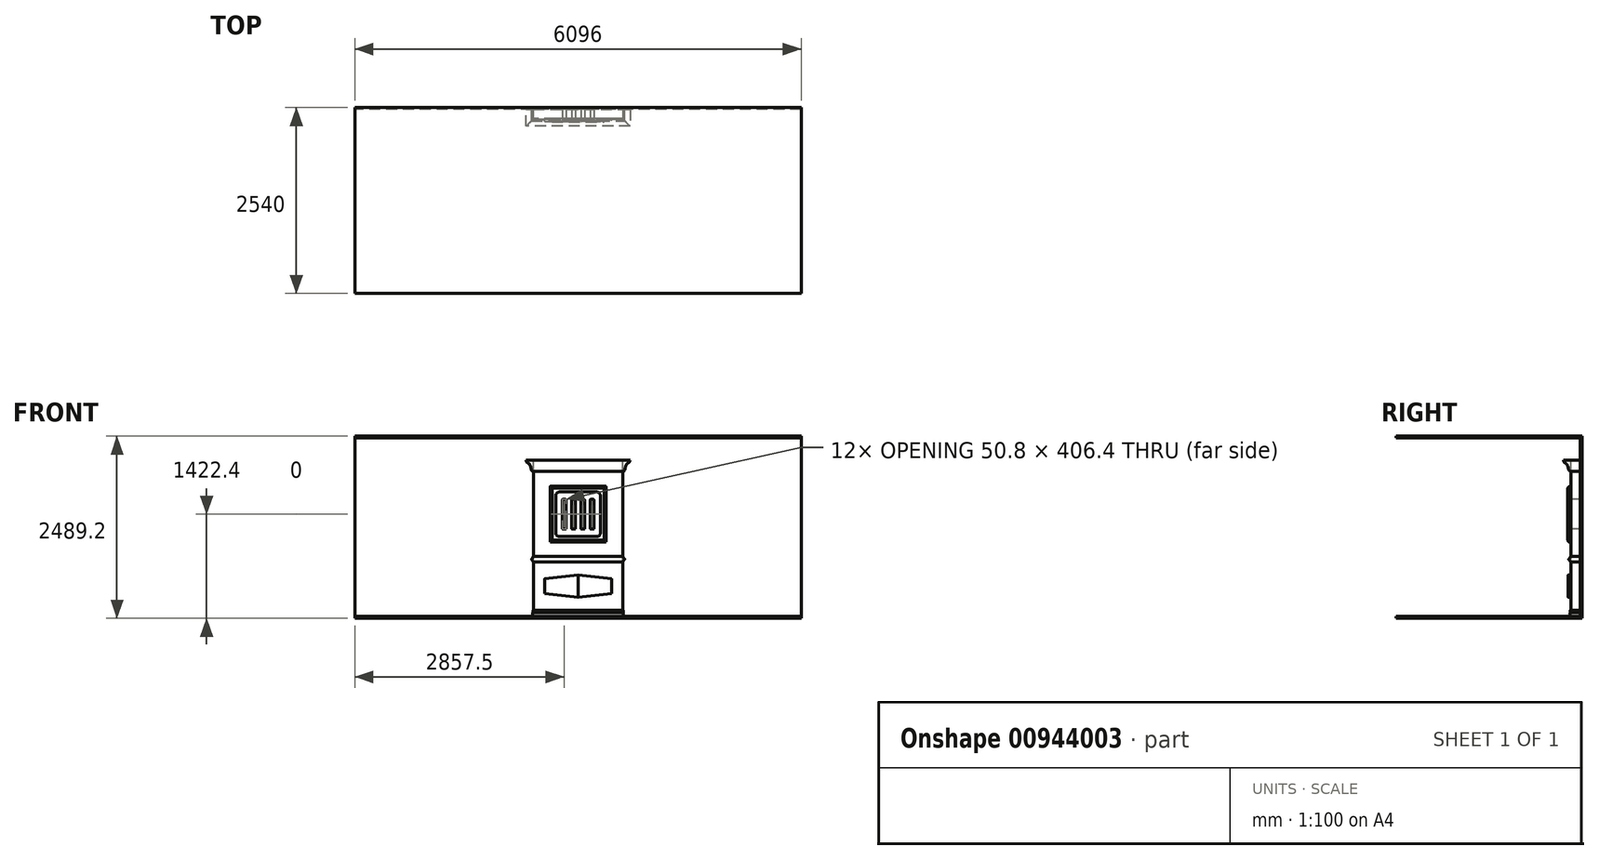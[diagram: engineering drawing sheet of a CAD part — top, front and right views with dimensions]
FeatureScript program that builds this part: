
annotation { "Feature Type Name" : "Feature", "Feature Type Description" : "" }
export const myFeature = defineFeature(function(context is Context, id is Id, definition is map)
    precondition{}
    {
        {
            var Q0;
            Q0=qCreatedBy(makeId("Front.planeOp"),FACE);
            var sketch = newSketch(context, id + "F0", { "sketchPlane" : qUnion([Q0])});
            skLineSegment(sketch, "E0.bottom", {"start": v(0, 0) * mm, "end": v(3657.6, 0) * mm});
            skLineSegment(sketch, "E0.top", {"start": v(0, 2438.4) * mm, "end": v(3657.6, 2438.4) * mm});
            skLineSegment(sketch, "E0.left", {"start": v(0, 0) * mm, "end": v(0, 2438.4) * mm});
            skLineSegment(sketch, "E0.right", {"start": v(3657.6, 0) * mm, "end": v(3657.6, 2438.4) * mm});
            skLineSegment(sketch, "E1.bottom", {"start": v(0, 0) * mm, "end": v(-2438.4, 0) * mm});
            skLineSegment(sketch, "E1.top", {"start": v(0, 2438.4) * mm, "end": v(-2438.4, 2438.4) * mm});
            skLineSegment(sketch, "E1.right", {"start": v(-2438.4, 0) * mm, "end": v(-2438.4, 2438.4) * mm});
            skSolve(sketch);
        }
        {
            var Q0;
            Q0=makeQuery(id+"F0.imprint","IMPRINT",FACE,{"disambiguationData":[TD([[makeQuery(id+"F0.imprint","IMPRINT",EDGE,{"derivedFrom":sQuery(id+"F0.wireOp",EDGE,"E1.bottom")}),-1.0]])]});
            var Q1;
            Q1=makeQuery(id+"F0.imprint","IMPRINT",FACE,{"disambiguationData":[TD([[makeQuery(id+"F0.imprint","IMPRINT",EDGE,{"derivedFrom":sQuery(id+"F0.wireOp",EDGE,"E0.bottom")}),1.0]])]});
            var Q2;
            Q2 = qConstructionFilter(qBodyType(qCreatedBy(id + "F0" ,EDGE), BodyType.WIRE), ConstructionObject.NO);
            extrude(context, id + "F1", {"entities" : qUnion([Q0, Q1]), "surfaceEntities" : qUnion([Q2]), "oppositeDirection" : true, "depth" : 25.4 * mm, "offsetDistance" : 25.4 * mm});
        }
        {
            var Q0;
            Q0=makeQuery(id+"F1.opExtrude","SWEPT_FACE",FACE,{"disambiguationData":[OSD([sQuery(id+"F0.wireOp",EDGE,"E0.top"),sQuery(id+"F0.wireOp",EDGE,"E1.top")])]});
            var sketch = newSketch(context, id + "F2", { "sketchPlane" : qUnion([Q0])});
            skLineSegment(sketch, "E2.bottom", {"start": v(-2438.4, 25.4) * mm, "end": v(3657.6, 25.4) * mm});
            skLineSegment(sketch, "E2.top", {"start": v(-2438.4, -2514.6) * mm, "end": v(3657.6, -2514.6) * mm});
            skLineSegment(sketch, "E2.left", {"start": v(-2438.4, 25.4) * mm, "end": v(-2438.4, -2514.6) * mm});
            skLineSegment(sketch, "E2.right", {"start": v(3657.6, 25.4) * mm, "end": v(3657.6, -2514.6) * mm});
            skSolve(sketch);
        }
        {
            var Q0;
            Q0 = qSketchRegion(id + "F2", true);
            extrude(context, id + "F3", {"entities" : qUnion([Q0]), "operationType" : NewBodyOperationType.ADD, "depth" : 25.4 * mm, "offsetDistance" : 25.4 * mm});
        }
        {
            var Q0;
            Q0=makeQuery(id+"F1.opExtrude","SWEPT_FACE",FACE,{"disambiguationData":[OSD([sQuery(id+"F0.wireOp",EDGE,"E0.bottom"),sQuery(id+"F0.wireOp",EDGE,"E1.bottom")])]});
            var sketch = newSketch(context, id + "F4", { "sketchPlane" : qUnion([Q0])});
            skLineSegment(sketch, "E3.bottom", {"start": v(-2438.4, -25.4) * mm, "end": v(3657.6, -25.4) * mm});
            skLineSegment(sketch, "E3.top", {"start": v(-2438.4, 2514.6) * mm, "end": v(3657.6, 2514.6) * mm});
            skLineSegment(sketch, "E3.left", {"start": v(-2438.4, -25.4) * mm, "end": v(-2438.4, 2514.6) * mm});
            skLineSegment(sketch, "E3.right", {"start": v(3657.6, -25.4) * mm, "end": v(3657.6, 2514.6) * mm});
            skSolve(sketch);
        }
        {
            var Q0;
            Q0 = qSketchRegion(id + "F4", true);
            extrude(context, id + "F5", {"entities" : qUnion([Q0]), "operationType" : NewBodyOperationType.ADD, "depth" : 25.4 * mm, "offsetDistance" : 25.4 * mm});
        }
        {
            var Q0;
            Q0=qCreatedBy(makeId("Front.planeOp"),FACE);
            var sketch = newSketch(context, id + "F6", { "sketchPlane" : qUnion([Q0])});
            skLineSegment(sketch, "E4.bottom", {"start": v(0, 0) * mm, "end": v(1219.2, 0) * mm});
            skLineSegment(sketch, "E4.top", {"start": v(0, 2133.6) * mm, "end": v(1219.2, 2133.6) * mm});
            skLineSegment(sketch, "E4.left", {"start": v(0, 0) * mm, "end": v(0, 2133.6) * mm});
            skLineSegment(sketch, "E4.right", {"start": v(1219.2, 0) * mm, "end": v(1219.2, 2133.6) * mm});
            skSolve(sketch);
        }
        {
            var Q0;
            Q0 = qSketchRegion(id + "F6", true);
            extrude(context, id + "F7", {"entities" : qUnion([Q0]), "depth" : 127 * mm, "offsetDistance" : 25.4 * mm});
        }
        {
            var Q0;
            Q0=makeQuery(id+"F7.opExtrude","CAP_FACE",FACE,{"disambiguationData":[OSD([sQuery(id+"F6.wireOp",EDGE,"E4.bottom"),sQuery(id+"F6.wireOp",EDGE,"E4.top"),sQuery(id+"F6.wireOp",EDGE,"E4.left"),sQuery(id+"F6.wireOp",EDGE,"E4.right")])],"isStart":false});
            var sketch = newSketch(context, id + "F8", { "sketchPlane" : qUnion([Q0])});
            skLineSegment(sketch, "E5.bottom", {"start": v(228.6, 1016) * mm, "end": v(990.6, 1016) * mm});
            skLineSegment(sketch, "E5.top", {"start": v(228.6, 1778) * mm, "end": v(990.6, 1778) * mm});
            skLineSegment(sketch, "E5.left", {"start": v(228.6, 1016) * mm, "end": v(228.6, 1778) * mm});
            skLineSegment(sketch, "E5.right", {"start": v(990.6, 1016) * mm, "end": v(990.6, 1778) * mm});
            skPoint(sketch, "E6", {"position": v(609.6, 1778) * mm});
            skPoint(sketch, "E7", {"position": v(609.6, 2133.6) * mm});
            skSolve(sketch);
        }
        {
            var Q0;
            Q0 = qSketchRegion(id + "F8", true);
            extrude(context, id + "F9", {"entities" : qUnion([Q0]), "depth" : 38.1 * mm, "offsetDistance" : 25.4 * mm});
        }
        {
            var Q0;
            Q0=makeQuery(id+"F7.opExtrude","SWEPT_FACE",FACE,{"disambiguationData":[OSD([sQuery(id+"F6.wireOp",EDGE,"E4.right")])]});
            var sketch = newSketch(context, id + "F10", { "sketchPlane" : qUnion([Q0])});
            skFitSpline(sketch, "E8", {"points": [v(-127, 1981.2) * mm, v(-163.97, 2045.51) * mm, v(-194.3, 2094.8) * mm, v(-228.6, 2133.6) * mm], "startDerivative": vector(-269.16, 89.83) * mm, "endDerivative": vector(-112.82, 304.77) * mm});
            skLineSegment(sketch, "E9", {"start": v(-228.6, 2133.6) * mm, "end": v(-127, 2133.6) * mm});
            skLineSegment(sketch, "E10", {"start": v(-127, 2133.6) * mm, "end": v(-127, 1981.2) * mm});
            skSolve(sketch);
        }
        {
            var Q0;
            Q0=makeQuery(id+"F10.imprint","IMPRINT",FACE,{"disambiguationData":[TD([[makeQuery(id+"F10.imprint","IMPRINT",EDGE,{"derivedFrom":sQuery(id+"F10.wireOp",EDGE,"E8")}),-1.0]])]});
            var Q1;
            Q1=makeQuery(id+"F7.opExtrude","CAP_EDGE",EDGE,{"disambiguationData":[OSD([sQuery(id+"F6.wireOp",EDGE,"E4.top")])],"isStart":false});
            var Q2;
            Q2=makeQuery(id+"F7.opExtrude","SWEPT_EDGE",EDGE,{"disambiguationData":[OSD([sQuery(id+"F6.wireOp",EDGE,"E4.top"),sQuery(id+"F6.wireOp",EDGE,"E4.left")])]});
            var Q3;
            Q3=makeQuery(id+"F7.opExtrude","SWEPT_EDGE",EDGE,{"disambiguationData":[OSD([sQuery(id+"F6.wireOp",EDGE,"E4.top"),sQuery(id+"F6.wireOp",EDGE,"E4.right")])]});
            sweep(context, id + "F11", {"profiles" : qUnion([Q0]), "path" : qUnion([Q1, Q2, Q3])});
        }
        {
            var Q0;
            Q0=makeQuery(id+"F9.opExtrude","SWEPT_FACE",FACE,{"disambiguationData":[OSD([sQuery(id+"F8.wireOp",EDGE,"E5.right")])]});
            var sketch = newSketch(context, id + "F12", { "sketchPlane" : qUnion([Q0])});
            skArc(sketch, "E11", {"start": v(-165.1, 1778) * mm, "mid": v(-153.94, 1804.94) * mm, "end": v(-127, 1816.1) * mm});
            skLineSegment(sketch, "E12", {"start": v(-127, 1816.1) * mm, "end": v(-127, 1778) * mm});
            skLineSegment(sketch, "E13", {"start": v(-165.1, 1778) * mm, "end": v(-127, 1778) * mm});
            skSolve(sketch);
        }
        {
            var Q0;
            Q0=makeQuery(id+"F9.opExtrude","CAP_FACE",FACE,{"disambiguationData":[OSD([sQuery(id+"F8.wireOp",EDGE,"E5.bottom"),sQuery(id+"F8.wireOp",EDGE,"E5.top"),sQuery(id+"F8.wireOp",EDGE,"E5.left"),sQuery(id+"F8.wireOp",EDGE,"E5.right")])],"isStart":false});
            var sketch = newSketch(context, id + "F13", { "sketchPlane" : qUnion([Q0])});
            skLineSegment(sketch, "E14.bottom", {"start": v(406.4, 1625.6) * mm, "end": v(431.8, 1625.6) * mm});
            skLineSegment(sketch, "E14.top", {"start": v(406.4, 1447.8) * mm, "end": v(431.8, 1447.8) * mm});
            skLineSegment(sketch, "E14.left", {"start": v(406.4, 1625.6) * mm, "end": v(406.4, 1447.8) * mm});
            skLineSegment(sketch, "E14.right", {"start": v(431.8, 1625.6) * mm, "end": v(431.8, 1447.8) * mm});
            skArc(sketch, "E15", {"start": v(431.8, 1625.6) * mm, "mid": v(419.1, 1638.3) * mm, "end": v(406.4, 1625.6) * mm});
            skArc(sketch, "E16", {"start": v(406.4, 1447.8) * mm, "mid": v(419.1, 1435.1) * mm, "end": v(431.8, 1447.8) * mm});
            skPoint(sketch, "E17", {"position": v(609.6, 1778) * mm});
            skLineSegment(sketch, "E18.0.1.0", {"start": v(406.4, 1346.2) * mm, "end": v(406.4, 1168.4) * mm});
            skArc(sketch, "E18.0.1.1", {"start": v(431.8, 1346.2) * mm, "mid": v(419.1, 1358.9) * mm, "end": v(406.4, 1346.2) * mm});
            skLineSegment(sketch, "E18.0.1.2", {"start": v(431.8, 1346.2) * mm, "end": v(431.8, 1168.4) * mm});
            skLineSegment(sketch, "E18.0.1.3", {"start": v(406.4, 1346.2) * mm, "end": v(431.8, 1346.2) * mm});
            skArc(sketch, "E18.0.1.4", {"start": v(406.4, 1168.4) * mm, "mid": v(419.1, 1155.7) * mm, "end": v(431.8, 1168.4) * mm});
            skLineSegment(sketch, "E18.0.1.5", {"start": v(406.4, 1168.4) * mm, "end": v(431.8, 1168.4) * mm});
            skLineSegment(sketch, "E18.1.0.0", {"start": v(482.6, 1625.6) * mm, "end": v(482.6, 1447.8) * mm});
            skArc(sketch, "E18.1.0.1", {"start": v(508, 1625.6) * mm, "mid": v(495.3, 1638.3) * mm, "end": v(482.6, 1625.6) * mm});
            skLineSegment(sketch, "E18.1.0.2", {"start": v(508, 1625.6) * mm, "end": v(508, 1447.8) * mm});
            skLineSegment(sketch, "E18.1.0.3", {"start": v(482.6, 1625.6) * mm, "end": v(508, 1625.6) * mm});
            skArc(sketch, "E18.1.0.4", {"start": v(482.6, 1447.8) * mm, "mid": v(495.3, 1435.1) * mm, "end": v(508, 1447.8) * mm});
            skLineSegment(sketch, "E18.1.0.5", {"start": v(482.6, 1447.8) * mm, "end": v(508, 1447.8) * mm});
            skLineSegment(sketch, "E18.1.1.0", {"start": v(482.6, 1346.2) * mm, "end": v(482.6, 1168.4) * mm});
            skArc(sketch, "E18.1.1.1", {"start": v(508, 1346.2) * mm, "mid": v(495.3, 1358.9) * mm, "end": v(482.6, 1346.2) * mm});
            skLineSegment(sketch, "E18.1.1.2", {"start": v(508, 1346.2) * mm, "end": v(508, 1168.4) * mm});
            skLineSegment(sketch, "E18.1.1.3", {"start": v(482.6, 1346.2) * mm, "end": v(508, 1346.2) * mm});
            skArc(sketch, "E18.1.1.4", {"start": v(482.6, 1168.4) * mm, "mid": v(495.3, 1155.7) * mm, "end": v(508, 1168.4) * mm});
            skLineSegment(sketch, "E18.1.1.5", {"start": v(482.6, 1168.4) * mm, "end": v(508, 1168.4) * mm});
            skLineSegment(sketch, "E18.2.0.0", {"start": v(558.8, 1625.6) * mm, "end": v(558.8, 1447.8) * mm});
            skArc(sketch, "E18.2.0.1", {"start": v(584.2, 1625.6) * mm, "mid": v(571.5, 1638.3) * mm, "end": v(558.8, 1625.6) * mm});
            skLineSegment(sketch, "E18.2.0.2", {"start": v(584.2, 1625.6) * mm, "end": v(584.2, 1447.8) * mm});
            skLineSegment(sketch, "E18.2.0.3", {"start": v(558.8, 1625.6) * mm, "end": v(584.2, 1625.6) * mm});
            skArc(sketch, "E18.2.0.4", {"start": v(558.8, 1447.8) * mm, "mid": v(571.5, 1435.1) * mm, "end": v(584.2, 1447.8) * mm});
            skLineSegment(sketch, "E18.2.0.5", {"start": v(558.8, 1447.8) * mm, "end": v(584.2, 1447.8) * mm});
            skLineSegment(sketch, "E18.2.1.0", {"start": v(558.8, 1346.2) * mm, "end": v(558.8, 1168.4) * mm});
            skArc(sketch, "E18.2.1.1", {"start": v(584.2, 1346.2) * mm, "mid": v(571.5, 1358.9) * mm, "end": v(558.8, 1346.2) * mm});
            skLineSegment(sketch, "E18.2.1.2", {"start": v(584.2, 1346.2) * mm, "end": v(584.2, 1168.4) * mm});
            skLineSegment(sketch, "E18.2.1.3", {"start": v(558.8, 1346.2) * mm, "end": v(584.2, 1346.2) * mm});
            skArc(sketch, "E18.2.1.4", {"start": v(558.8, 1168.4) * mm, "mid": v(571.5, 1155.7) * mm, "end": v(584.2, 1168.4) * mm});
            skLineSegment(sketch, "E18.2.1.5", {"start": v(558.8, 1168.4) * mm, "end": v(584.2, 1168.4) * mm});
            skLineSegment(sketch, "E18.3.0.0", {"start": v(635, 1625.6) * mm, "end": v(635, 1447.8) * mm});
            skArc(sketch, "E18.3.0.1", {"start": v(660.4, 1625.6) * mm, "mid": v(647.7, 1638.3) * mm, "end": v(635, 1625.6) * mm});
            skLineSegment(sketch, "E18.3.0.2", {"start": v(660.4, 1625.6) * mm, "end": v(660.4, 1447.8) * mm});
            skLineSegment(sketch, "E18.3.0.3", {"start": v(635, 1625.6) * mm, "end": v(660.4, 1625.6) * mm});
            skArc(sketch, "E18.3.0.4", {"start": v(635, 1447.8) * mm, "mid": v(647.7, 1435.1) * mm, "end": v(660.4, 1447.8) * mm});
            skLineSegment(sketch, "E18.3.0.5", {"start": v(635, 1447.8) * mm, "end": v(660.4, 1447.8) * mm});
            skLineSegment(sketch, "E18.3.1.0", {"start": v(635, 1346.2) * mm, "end": v(635, 1168.4) * mm});
            skArc(sketch, "E18.3.1.1", {"start": v(660.4, 1346.2) * mm, "mid": v(647.7, 1358.9) * mm, "end": v(635, 1346.2) * mm});
            skLineSegment(sketch, "E18.3.1.2", {"start": v(660.4, 1346.2) * mm, "end": v(660.4, 1168.4) * mm});
            skLineSegment(sketch, "E18.3.1.3", {"start": v(635, 1346.2) * mm, "end": v(660.4, 1346.2) * mm});
            skArc(sketch, "E18.3.1.4", {"start": v(635, 1168.4) * mm, "mid": v(647.7, 1155.7) * mm, "end": v(660.4, 1168.4) * mm});
            skLineSegment(sketch, "E18.3.1.5", {"start": v(635, 1168.4) * mm, "end": v(660.4, 1168.4) * mm});
            skLineSegment(sketch, "E18.4.0.0", {"start": v(711.2, 1625.6) * mm, "end": v(711.2, 1447.8) * mm});
            skArc(sketch, "E18.4.0.1", {"start": v(736.6, 1625.6) * mm, "mid": v(723.9, 1638.3) * mm, "end": v(711.2, 1625.6) * mm});
            skLineSegment(sketch, "E18.4.0.2", {"start": v(736.6, 1625.6) * mm, "end": v(736.6, 1447.8) * mm});
            skLineSegment(sketch, "E18.4.0.3", {"start": v(711.2, 1625.6) * mm, "end": v(736.6, 1625.6) * mm});
            skArc(sketch, "E18.4.0.4", {"start": v(711.2, 1447.8) * mm, "mid": v(723.9, 1435.1) * mm, "end": v(736.6, 1447.8) * mm});
            skLineSegment(sketch, "E18.4.0.5", {"start": v(711.2, 1447.8) * mm, "end": v(736.6, 1447.8) * mm});
            skLineSegment(sketch, "E18.4.1.0", {"start": v(711.2, 1346.2) * mm, "end": v(711.2, 1168.4) * mm});
            skArc(sketch, "E18.4.1.1", {"start": v(736.6, 1346.2) * mm, "mid": v(723.9, 1358.9) * mm, "end": v(711.2, 1346.2) * mm});
            skLineSegment(sketch, "E18.4.1.2", {"start": v(736.6, 1346.2) * mm, "end": v(736.6, 1168.4) * mm});
            skLineSegment(sketch, "E18.4.1.3", {"start": v(711.2, 1346.2) * mm, "end": v(736.6, 1346.2) * mm});
            skArc(sketch, "E18.4.1.4", {"start": v(711.2, 1168.4) * mm, "mid": v(723.9, 1155.7) * mm, "end": v(736.6, 1168.4) * mm});
            skLineSegment(sketch, "E18.4.1.5", {"start": v(711.2, 1168.4) * mm, "end": v(736.6, 1168.4) * mm});
            skLineSegment(sketch, "E18.5.0.0", {"start": v(787.4, 1625.6) * mm, "end": v(787.4, 1447.8) * mm});
            skArc(sketch, "E18.5.0.1", {"start": v(812.8, 1625.6) * mm, "mid": v(800.1, 1638.3) * mm, "end": v(787.4, 1625.6) * mm});
            skLineSegment(sketch, "E18.5.0.2", {"start": v(812.8, 1625.6) * mm, "end": v(812.8, 1447.8) * mm});
            skLineSegment(sketch, "E18.5.0.3", {"start": v(787.4, 1625.6) * mm, "end": v(812.8, 1625.6) * mm});
            skArc(sketch, "E18.5.0.4", {"start": v(787.4, 1447.8) * mm, "mid": v(800.1, 1435.1) * mm, "end": v(812.8, 1447.8) * mm});
            skLineSegment(sketch, "E18.5.0.5", {"start": v(787.4, 1447.8) * mm, "end": v(812.8, 1447.8) * mm});
            skLineSegment(sketch, "E18.5.1.0", {"start": v(787.4, 1346.2) * mm, "end": v(787.4, 1168.4) * mm});
            skArc(sketch, "E18.5.1.1", {"start": v(812.8, 1346.2) * mm, "mid": v(800.1, 1358.9) * mm, "end": v(787.4, 1346.2) * mm});
            skLineSegment(sketch, "E18.5.1.2", {"start": v(812.8, 1346.2) * mm, "end": v(812.8, 1168.4) * mm});
            skLineSegment(sketch, "E18.5.1.3", {"start": v(787.4, 1346.2) * mm, "end": v(812.8, 1346.2) * mm});
            skArc(sketch, "E18.5.1.4", {"start": v(787.4, 1168.4) * mm, "mid": v(800.1, 1155.7) * mm, "end": v(812.8, 1168.4) * mm});
            skLineSegment(sketch, "E18.5.1.5", {"start": v(787.4, 1168.4) * mm, "end": v(812.8, 1168.4) * mm});
            skLineSegment(sketch, "E18.direction1", {"start": v(406.4, 1447.8) * mm, "end": v(482.6, 1447.8) * mm, "construction": true});
            skLineSegment(sketch, "E18.direction2", {"start": v(406.4, 1447.8) * mm, "end": v(406.4, 1168.4) * mm, "construction": true});
            skLineSegment(sketch, "E19", {"start": v(584.2, 1536.7) * mm, "end": v(635, 1536.7) * mm, "construction": true});
            skPoint(sketch, "E20", {"position": v(609.6, 1536.7) * mm});
            skLineSegment(sketch, "E21", {"start": v(419.1, 1447.8) * mm, "end": v(419.1, 1346.2) * mm, "construction": true});
            skPoint(sketch, "E22", {"position": v(419.1, 1397) * mm});
            skPoint(sketch, "E23", {"position": v(228.6, 1397) * mm});
            skSolve(sketch);
        }
        {
            var Q0;
            Q0=makeQuery(id+"F9.opExtrude","CAP_FACE",FACE,{"disambiguationData":[OSD([sQuery(id+"F8.wireOp",EDGE,"E5.bottom"),sQuery(id+"F8.wireOp",EDGE,"E5.top"),sQuery(id+"F8.wireOp",EDGE,"E5.left"),sQuery(id+"F8.wireOp",EDGE,"E5.right")])],"isStart":false});
            var sketch = newSketch(context, id + "F14", { "sketchPlane" : qUnion([Q0])});
            skLineSegment(sketch, "E24.bottom", {"start": v(438.15, 1600.2) * mm, "end": v(400.05, 1600.2) * mm});
            skLineSegment(sketch, "E24.top", {"start": v(438.15, 1193.8) * mm, "end": v(400.05, 1193.8) * mm});
            skLineSegment(sketch, "E24.left", {"start": v(444.5, 1593.85) * mm, "end": v(444.5, 1200.15) * mm});
            skLineSegment(sketch, "E24.right", {"start": v(393.7, 1593.85) * mm, "end": v(393.7, 1200.15) * mm});
            skPoint(sketch, "E24.middle", {"position": v(419.1, 1397) * mm});
            skLineSegment(sketch, "E25.1.0.0", {"start": v(565.15, 1193.8) * mm, "end": v(527.05, 1193.8) * mm});
            skLineSegment(sketch, "E25.1.0.1", {"start": v(565.15, 1600.2) * mm, "end": v(527.05, 1600.2) * mm});
            skPoint(sketch, "E25.1.0.2", {"position": v(546.1, 1397) * mm});
            skLineSegment(sketch, "E25.1.0.3", {"start": v(520.7, 1593.85) * mm, "end": v(520.7, 1200.15) * mm});
            skLineSegment(sketch, "E25.1.0.4", {"start": v(571.5, 1593.85) * mm, "end": v(571.5, 1200.15) * mm});
            skLineSegment(sketch, "E25.2.0.0", {"start": v(692.15, 1193.8) * mm, "end": v(654.05, 1193.8) * mm});
            skLineSegment(sketch, "E25.2.0.1", {"start": v(692.15, 1600.2) * mm, "end": v(654.05, 1600.2) * mm});
            skPoint(sketch, "E25.2.0.2", {"position": v(673.1, 1397) * mm});
            skLineSegment(sketch, "E25.2.0.3", {"start": v(647.7, 1593.85) * mm, "end": v(647.7, 1200.15) * mm});
            skLineSegment(sketch, "E25.2.0.4", {"start": v(698.5, 1593.85) * mm, "end": v(698.5, 1200.15) * mm});
            skLineSegment(sketch, "E25.3.0.0", {"start": v(819.15, 1193.8) * mm, "end": v(781.05, 1193.8) * mm});
            skLineSegment(sketch, "E25.3.0.1", {"start": v(819.15, 1600.2) * mm, "end": v(781.05, 1600.2) * mm});
            skPoint(sketch, "E25.3.0.2", {"position": v(800.1, 1397) * mm});
            skLineSegment(sketch, "E25.3.0.3", {"start": v(774.7, 1593.85) * mm, "end": v(774.7, 1200.15) * mm});
            skLineSegment(sketch, "E25.3.0.4", {"start": v(825.5, 1593.85) * mm, "end": v(825.5, 1200.15) * mm});
            skLineSegment(sketch, "E25.direction1", {"start": v(393.7, 1193.8) * mm, "end": v(520.7, 1193.8) * mm, "construction": true});
            skLineSegment(sketch, "E26", {"start": v(546.1, 1397) * mm, "end": v(673.1, 1397) * mm, "construction": true});
            skPoint(sketch, "E27", {"position": v(609.6, 1397) * mm});
            skPoint(sketch, "E28.visualSharp", {"position": v(393.7, 1600.2) * mm});
            skArc(sketch, "E28.filletArc", {"start": v(400.05, 1600.2) * mm, "mid": v(395.56, 1598.34) * mm, "end": v(393.7, 1593.85) * mm});
            skPoint(sketch, "E29.visualSharp", {"position": v(444.5, 1600.2) * mm});
            skArc(sketch, "E29.filletArc", {"start": v(444.5, 1593.85) * mm, "mid": v(442.64, 1598.34) * mm, "end": v(438.15, 1600.2) * mm});
            skPoint(sketch, "E30.visualSharp", {"position": v(393.7, 1193.8) * mm});
            skArc(sketch, "E30.filletArc", {"start": v(393.7, 1200.15) * mm, "mid": v(395.56, 1195.66) * mm, "end": v(400.05, 1193.8) * mm});
            skPoint(sketch, "E31.visualSharp", {"position": v(444.5, 1193.8) * mm});
            skArc(sketch, "E31.filletArc", {"start": v(438.15, 1193.8) * mm, "mid": v(442.64, 1195.66) * mm, "end": v(444.5, 1200.15) * mm});
            skPoint(sketch, "E32.visualSharp", {"position": v(520.7, 1193.8) * mm});
            skArc(sketch, "E32.filletArc", {"start": v(520.7, 1200.15) * mm, "mid": v(522.56, 1195.66) * mm, "end": v(527.05, 1193.8) * mm});
            skPoint(sketch, "E33.visualSharp", {"position": v(571.5, 1193.8) * mm});
            skArc(sketch, "E33.filletArc", {"start": v(565.15, 1193.8) * mm, "mid": v(569.64, 1195.66) * mm, "end": v(571.5, 1200.15) * mm});
            skPoint(sketch, "E34.visualSharp", {"position": v(520.7, 1600.2) * mm});
            skArc(sketch, "E34.filletArc", {"start": v(527.05, 1600.2) * mm, "mid": v(522.56, 1598.34) * mm, "end": v(520.7, 1593.85) * mm});
            skPoint(sketch, "E35.visualSharp", {"position": v(571.5, 1600.2) * mm});
            skArc(sketch, "E35.filletArc", {"start": v(571.5, 1593.85) * mm, "mid": v(569.64, 1598.34) * mm, "end": v(565.15, 1600.2) * mm});
            skPoint(sketch, "E36.visualSharp", {"position": v(647.7, 1600.2) * mm});
            skArc(sketch, "E36.filletArc", {"start": v(654.05, 1600.2) * mm, "mid": v(649.56, 1598.34) * mm, "end": v(647.7, 1593.85) * mm});
            skPoint(sketch, "E37.visualSharp", {"position": v(698.5, 1600.2) * mm});
            skArc(sketch, "E37.filletArc", {"start": v(698.5, 1593.85) * mm, "mid": v(696.64, 1598.34) * mm, "end": v(692.15, 1600.2) * mm});
            skPoint(sketch, "E38.visualSharp", {"position": v(698.5, 1193.8) * mm});
            skArc(sketch, "E38.filletArc", {"start": v(692.15, 1193.8) * mm, "mid": v(696.64, 1195.66) * mm, "end": v(698.5, 1200.15) * mm});
            skPoint(sketch, "E39.visualSharp", {"position": v(647.7, 1193.8) * mm});
            skArc(sketch, "E39.filletArc", {"start": v(647.7, 1200.15) * mm, "mid": v(649.56, 1195.66) * mm, "end": v(654.05, 1193.8) * mm});
            skPoint(sketch, "E40.visualSharp", {"position": v(774.7, 1193.8) * mm});
            skArc(sketch, "E40.filletArc", {"start": v(774.7, 1200.15) * mm, "mid": v(776.56, 1195.66) * mm, "end": v(781.05, 1193.8) * mm});
            skPoint(sketch, "E41.visualSharp", {"position": v(825.5, 1193.8) * mm});
            skArc(sketch, "E41.filletArc", {"start": v(819.15, 1193.8) * mm, "mid": v(823.64, 1195.66) * mm, "end": v(825.5, 1200.15) * mm});
            skPoint(sketch, "E42.visualSharp", {"position": v(825.5, 1600.2) * mm});
            skArc(sketch, "E42.filletArc", {"start": v(825.5, 1593.85) * mm, "mid": v(823.64, 1598.34) * mm, "end": v(819.15, 1600.2) * mm});
            skPoint(sketch, "E43.visualSharp", {"position": v(774.7, 1600.2) * mm});
            skArc(sketch, "E43.filletArc", {"start": v(781.05, 1600.2) * mm, "mid": v(776.56, 1598.34) * mm, "end": v(774.7, 1593.85) * mm});
            skSolve(sketch);
        }
        {
            var Q0;
            Q0 = qSketchRegion(id + "F14", true);
            extrude(context, id + "F15", {"entities" : qUnion([Q0]), "operationType" : NewBodyOperationType.REMOVE, "endBound" : BoundingType.THROUGH_ALL, "oppositeDirection" : true, "depth" : 25.4 * mm, "offsetDistance" : 25.4 * mm});
        }
        {
            var Q0;
            Q0=makeQuery(id+"F9.opExtrude","CAP_EDGE",EDGE,{"disambiguationData":[OSD([sQuery(id+"F8.wireOp",EDGE,"E5.right")])],"isStart":false});
            var Q1;
            Q1=makeQuery(id+"F9.opExtrude","CAP_EDGE",EDGE,{"disambiguationData":[OSD([sQuery(id+"F8.wireOp",EDGE,"E5.top")])],"isStart":false});
            var Q2;
            Q2=makeQuery(id+"F9.opExtrude","CAP_EDGE",EDGE,{"disambiguationData":[OSD([sQuery(id+"F8.wireOp",EDGE,"E5.left")])],"isStart":false});
            var Q3;
            Q3=makeQuery(id+"F9.opExtrude","CAP_EDGE",EDGE,{"disambiguationData":[OSD([sQuery(id+"F8.wireOp",EDGE,"E5.bottom")])],"isStart":false});
            var Q4;
            Q4=makeQuery(id+"FaYRPH6JfX0Mlm0_8.opExtrude","CAP_EDGE",EDGE,{"disambiguationData":[OSD([sQuery(id+"FZfI06hDJg0UXKs_8.wireOp",EDGE,"63A7O8QR-ZqBt-5VyV-VJpw-3I6lRBvDDIq9.bottom")])],"isStart":false});
            var Q5;
            Q5=makeQuery(id+"FaYRPH6JfX0Mlm0_8.opExtrude","CAP_EDGE",EDGE,{"disambiguationData":[OSD([sQuery(id+"FZfI06hDJg0UXKs_8.wireOp",EDGE,"63A7O8QR-ZqBt-5VyV-VJpw-3I6lRBvDDIq9.left")])],"isStart":false});
            var Q6;
            Q6=makeQuery(id+"FaYRPH6JfX0Mlm0_8.opExtrude","CAP_EDGE",EDGE,{"disambiguationData":[OSD([sQuery(id+"FZfI06hDJg0UXKs_8.wireOp",EDGE,"63A7O8QR-ZqBt-5VyV-VJpw-3I6lRBvDDIq9.top")])],"isStart":true});
            var Q7;
            Q7=makeQuery(id+"FaYRPH6JfX0Mlm0_8.opExtrude","CAP_EDGE",EDGE,{"disambiguationData":[OSD([sQuery(id+"FZfI06hDJg0UXKs_8.wireOp",EDGE,"63A7O8QR-ZqBt-5VyV-VJpw-3I6lRBvDDIq9.right")])],"isStart":false});
            fillet(context, id + "F16", {"entities" : qUnion([Q0, Q1, Q2, Q3, Q4, Q5, Q6, Q7]), "radius" : 25.4 * mm, "tangentPropagation" : true, "defaultsChanged" : true, "vertexSettings" : [], "allowEdgeOverflow" : false});
        }
        {
            var Q0;
            Q0=makeQuery(id+"F7.opExtrude","SWEPT_FACE",FACE,{"disambiguationData":[OSD([sQuery(id+"F6.wireOp",EDGE,"E4.right")])]});
            var sketch = newSketch(context, id + "F17", { "sketchPlane" : qUnion([Q0])});
            skFitSpline(sketch, "E44", {"points": [v(-127, 820.64) * mm, v(-138.27, 801.26) * mm, v(-153.99, 782.54) * mm, v(-138.27, 763.82) * mm, v(-127, 744.44) * mm], "startDerivative": vector(-96, -20.35) * mm, "endDerivative": vector(138.24, -117.77) * mm});
            skLineSegment(sketch, "E45", {"start": v(-127, 820.64) * mm, "end": v(-127, 744.44) * mm});
            skPoint(sketch, "E46", {"position": v(-127, 782.54) * mm});
            skLineSegment(sketch, "E47", {"start": v(-153.99, 782.54) * mm, "end": v(-127, 782.54) * mm, "construction": true});
            skLineSegment(sketch, "E48", {"start": v(-138.27, 801.26) * mm, "end": v(-138.27, 763.82) * mm, "construction": true});
            skPoint(sketch, "E49", {"position": v(-138.27, 782.54) * mm});
            skLineSegment(sketch, "E50", {"start": v(-153.99, 782.54) * mm, "end": v(-127, 782.54) * mm});
            skSolve(sketch);
        }
        {
            var Q0;
            Q0=makeQuery(id+"F17.imprint","IMPRINT",FACE,{"disambiguationData":[TD([[makeQuery(id+"F17.imprint","IMPRINT",EDGE,{"derivedFrom":sQuery(id+"F17.wireOp",EDGE,"E44")}),1.0]])]});
            var Q1;
            Q1=makeQuery(id+"F7.opExtrude","CAP_EDGE",EDGE,{"disambiguationData":[OSD([sQuery(id+"F6.wireOp",EDGE,"E4.bottom")])],"isStart":false});
            var Q2;
            Q2=makeQuery(id+"F7.opExtrude","SWEPT_EDGE",EDGE,{"disambiguationData":[OSD([sQuery(id+"F6.wireOp",EDGE,"E4.bottom"),sQuery(id+"F6.wireOp",EDGE,"E4.left")])]});
            var Q3;
            Q3=makeQuery(id+"F7.opExtrude","SWEPT_EDGE",EDGE,{"disambiguationData":[OSD([sQuery(id+"F6.wireOp",EDGE,"E4.bottom"),sQuery(id+"F6.wireOp",EDGE,"E4.right")])]});
            sweep(context, id + "F18", {"profiles" : qUnion([Q0]), "path" : qUnion([Q1, Q2, Q3])});
        }
        {
            var Q0;
            Q0=makeQuery(id+"F7.opExtrude","SWEPT_FACE",FACE,{"disambiguationData":[OSD([sQuery(id+"F6.wireOp",EDGE,"E4.right")])]});
            var sketch = newSketch(context, id + "F19", { "sketchPlane" : qUnion([Q0])});
            skLineSegment(sketch, "E51", {"start": v(-127, 0) * mm, "end": v(-136.53, 0) * mm});
            skLineSegment(sketch, "E52", {"start": v(-136.53, 0) * mm, "end": v(-136.53, 50.8) * mm});
            skFitSpline(sketch, "E53", {"points": [v(-136.53, 50.8) * mm, v(-133.18, 67.69) * mm, v(-134.44, 77.27) * mm, v(-127, 85.73) * mm], "startDerivative": vector(35.03, 31.73) * mm, "endDerivative": vector(59.01, 5.94) * mm});
            skLineSegment(sketch, "E54", {"start": v(-127, 0) * mm, "end": v(-127, 85.73) * mm});
            skSolve(sketch);
        }
        {
            var Q0;
            Q0=makeQuery(id+"F19.imprint","IMPRINT",FACE,{"disambiguationData":[TD([[makeQuery(id+"F19.imprint","IMPRINT",EDGE,{"derivedFrom":sQuery(id+"F19.wireOp",EDGE,"E51")}),-1.0]])]});
            var Q1;
            Q1=makeQuery(id+"F7.opExtrude","CAP_EDGE",EDGE,{"disambiguationData":[OSD([sQuery(id+"F6.wireOp",EDGE,"E4.bottom")])],"isStart":false});
            var Q2;
            Q2=makeQuery(id+"F7.opExtrude","SWEPT_EDGE",EDGE,{"disambiguationData":[OSD([sQuery(id+"F6.wireOp",EDGE,"E4.bottom"),sQuery(id+"F6.wireOp",EDGE,"E4.right")])]});
            var Q3;
            Q3=makeQuery(id+"F7.opExtrude","SWEPT_EDGE",EDGE,{"disambiguationData":[OSD([sQuery(id+"F6.wireOp",EDGE,"E4.bottom"),sQuery(id+"F6.wireOp",EDGE,"E4.left")])]});
            sweep(context, id + "F20", {"profiles" : qUnion([Q0]), "path" : qUnion([Q1, Q2, Q3])});
        }
        {
            var Q0;
            Q0=makeQuery(id+"F7.opExtrude","CAP_FACE",FACE,{"disambiguationData":[OSD([sQuery(id+"F6.wireOp",EDGE,"E4.bottom"),sQuery(id+"F6.wireOp",EDGE,"E4.top"),sQuery(id+"F6.wireOp",EDGE,"E4.left"),sQuery(id+"F6.wireOp",EDGE,"E4.right")])],"isStart":false});
            var sketch = newSketch(context, id + "F21", { "sketchPlane" : qUnion([Q0])});
            skLineSegment(sketch, "E55", {"start": v(152.4, 567.48) * mm, "end": v(1066.8, 567.48) * mm, "construction": true});
            skLineSegment(sketch, "E56", {"start": v(1066.8, 567.48) * mm, "end": v(1066.8, 262.68) * mm, "construction": true});
            skLineSegment(sketch, "E57", {"start": v(1066.8, 262.68) * mm, "end": v(152.4, 262.68) * mm, "construction": true});
            skLineSegment(sketch, "E58", {"start": v(152.4, 262.68) * mm, "end": v(152.4, 567.48) * mm, "construction": true});
            skLineSegment(sketch, "E59", {"start": v(609.6, 567.48) * mm, "end": v(609.6, 262.68) * mm});
            skLineSegment(sketch, "E60", {"start": v(1183.93, 85.73) * mm, "end": v(1183.93, 744.44) * mm, "construction": true});
            skPoint(sketch, "E61", {"position": v(1066.8, 415.08) * mm});
            skPoint(sketch, "E62", {"position": v(1183.93, 415.08) * mm});
            skLineSegment(sketch, "E63", {"start": v(609.6, 567.48) * mm, "end": v(152.4, 516.68) * mm});
            skLineSegment(sketch, "E64", {"start": v(152.4, 516.68) * mm, "end": v(152.4, 313.48) * mm});
            skLineSegment(sketch, "E65", {"start": v(152.4, 313.48) * mm, "end": v(609.6, 262.68) * mm});
            skLineSegment(sketch, "E66", {"start": v(609.6, 262.68) * mm, "end": v(1066.8, 313.48) * mm});
            skLineSegment(sketch, "E67", {"start": v(1066.8, 313.48) * mm, "end": v(1066.8, 516.68) * mm});
            skLineSegment(sketch, "E68", {"start": v(1066.8, 516.68) * mm, "end": v(609.6, 567.48) * mm});
            skSolve(sketch);
        }
        {
            var Q0;
            Q0=makeQuery(id+"F21.imprint","IMPRINT",FACE,{"disambiguationData":[TD([[makeQuery(id+"F21.imprint","IMPRINT",EDGE,{"derivedFrom":sQuery(id+"F21.wireOp",EDGE,"E59")}),-1.0]])]});
            var Q1;
            Q1=makeQuery(id+"F9.opExtrude","CAP_FACE",FACE,{"disambiguationData":[OSD([sQuery(id+"F8.wireOp",EDGE,"E5.bottom"),sQuery(id+"F8.wireOp",EDGE,"E5.top"),sQuery(id+"F8.wireOp",EDGE,"E5.left"),sQuery(id+"F8.wireOp",EDGE,"E5.right")])],"isStart":false});
            extrude(context, id + "F22", {"entities" : qUnion([Q0]), "endBound" : BoundingType.UP_TO_SURFACE, "depth" : 25.4 * mm, "endBoundEntityFace" : qUnion([Q1]), "offsetDistance" : 25.4 * mm});
        }
        {
            var Q0;
            Q0=makeQuery(id+"F21.imprint","IMPRINT",FACE,{"disambiguationData":[TD([[makeQuery(id+"F21.imprint","IMPRINT",EDGE,{"derivedFrom":sQuery(id+"F21.wireOp",EDGE,"E59")}),1.0]])]});
            extrude(context, id + "F23", {"entities" : qUnion([Q0]), "depth" : 25.4 * mm, "offsetDistance" : 25.4 * mm});
        }
        {
            var Q0;
            Q0=makeQuery(id+"F22.opExtrude","CAP_EDGE",EDGE,{"disambiguationData":[OSD([sQuery(id+"F21.wireOp",EDGE,"E63")])],"isStart":false});
            var Q1;
            Q1=makeQuery(id+"F22.opExtrude","CAP_EDGE",EDGE,{"disambiguationData":[OSD([sQuery(id+"F21.wireOp",EDGE,"E65")])],"isStart":false});
            var Q2;
            Q2=makeQuery(id+"F22.opExtrude","CAP_EDGE",EDGE,{"disambiguationData":[OSD([sQuery(id+"F21.wireOp",EDGE,"E66")])],"isStart":false});
            var Q3;
            Q3=makeQuery(id+"F22.opExtrude","CAP_EDGE",EDGE,{"disambiguationData":[OSD([sQuery(id+"F21.wireOp",EDGE,"E67")])],"isStart":false});
            var Q4;
            Q4=makeQuery(id+"F22.opExtrude","CAP_EDGE",EDGE,{"disambiguationData":[OSD([sQuery(id+"F21.wireOp",EDGE,"E68")])],"isStart":false});
            var Q5;
            Q5=makeQuery(id+"F22.opExtrude","CAP_EDGE",EDGE,{"disambiguationData":[OSD([sQuery(id+"F21.wireOp",EDGE,"E64")])],"isStart":false});
            var Q6;
            Q6=makeQuery(id+"F23.opExtrude","CAP_EDGE",EDGE,{"disambiguationData":[OSD([sQuery(id+"F21.wireOp",EDGE,"E68")])],"isStart":false});
            var Q7;
            Q7=makeQuery(id+"F23.opExtrude","CAP_EDGE",EDGE,{"disambiguationData":[OSD([sQuery(id+"F21.wireOp",EDGE,"E67")])],"isStart":false});
            var Q8;
            Q8=makeQuery(id+"F23.opExtrude","CAP_EDGE",EDGE,{"disambiguationData":[OSD([sQuery(id+"F21.wireOp",EDGE,"E66")])],"isStart":false});
            fillet(context, id + "F24", {"entities" : qUnion([Q0, Q1, Q2, Q3, Q4, Q5, Q6, Q7, Q8]), "radius" : 5.08 * mm, "tangentPropagation" : true, "allowEdgeOverflow" : false});
        }
        {
            var Q0;
            Q0=makeQuery(id+"F9.opExtrude","CAP_FACE",FACE,{"disambiguationData":[OSD([sQuery(id+"F8.wireOp",EDGE,"E5.bottom"),sQuery(id+"F8.wireOp",EDGE,"E5.top"),sQuery(id+"F8.wireOp",EDGE,"E5.left"),sQuery(id+"F8.wireOp",EDGE,"E5.right")])],"isStart":false});
            var sketch = newSketch(context, id + "F25", { "sketchPlane" : qUnion([Q0])});
            skLineSegment(sketch, "E69.bottom", {"start": v(965.2, 1752.6) * mm, "end": v(254, 1752.6) * mm});
            skLineSegment(sketch, "E69.top", {"start": v(965.2, 1041.4) * mm, "end": v(254, 1041.4) * mm});
            skLineSegment(sketch, "E69.left", {"start": v(965.2, 1752.6) * mm, "end": v(965.2, 1041.4) * mm});
            skLineSegment(sketch, "E69.right", {"start": v(254, 1752.6) * mm, "end": v(254, 1041.4) * mm});
            skPoint(sketch, "E69.middle", {"position": v(609.6, 1397) * mm});
            skPoint(sketch, "E69.middle.positionSnap0", {"position": v(571.5, 1397) * mm});
            skPoint(sketch, "E69.middle.positionSnap1", {"position": v(609.6, 1752.6) * mm});
            skPoint(sketch, "E69.centerSnap0", {"position": v(571.5, 1397) * mm});
            skPoint(sketch, "E69.centerSnap1", {"position": v(609.6, 1752.6) * mm});
            skLineSegment(sketch, "E70.0", {"start": v(863.6, 1701.8) * mm, "end": v(355.6, 1701.8) * mm});
            skLineSegment(sketch, "E70.1", {"start": v(914.4, 1651) * mm, "end": v(914.4, 1143) * mm});
            skLineSegment(sketch, "E70.2", {"start": v(863.6, 1092.2) * mm, "end": v(355.6, 1092.2) * mm});
            skLineSegment(sketch, "E70.3", {"start": v(304.8, 1651) * mm, "end": v(304.8, 1143) * mm});
            skPoint(sketch, "E71.visualSharp", {"position": v(304.8, 1701.8) * mm});
            skArc(sketch, "E71.filletArc", {"start": v(355.6, 1701.8) * mm, "mid": v(319.68, 1686.92) * mm, "end": v(304.8, 1651) * mm});
            skPoint(sketch, "E72.visualSharp", {"position": v(304.8, 1092.2) * mm});
            skArc(sketch, "E72.filletArc", {"start": v(304.8, 1143) * mm, "mid": v(319.68, 1107.08) * mm, "end": v(355.6, 1092.2) * mm});
            skPoint(sketch, "E73.visualSharp", {"position": v(914.4, 1092.2) * mm});
            skArc(sketch, "E73.filletArc", {"start": v(863.6, 1092.2) * mm, "mid": v(899.52, 1107.08) * mm, "end": v(914.4, 1143) * mm});
            skPoint(sketch, "E74.visualSharp", {"position": v(914.4, 1701.8) * mm});
            skArc(sketch, "E74.filletArc", {"start": v(914.4, 1651) * mm, "mid": v(899.52, 1686.92) * mm, "end": v(863.6, 1701.8) * mm});
            skSolve(sketch);
        }
        {
            var Q0;
            Q0 = qSketchRegion(id + "F25", true);
            extrude(context, id + "F26", {"entities" : qUnion([Q0]), "operationType" : NewBodyOperationType.ADD, "depth" : 6.35 * mm, "offsetDistance" : 25.4 * mm});
        }
    });
